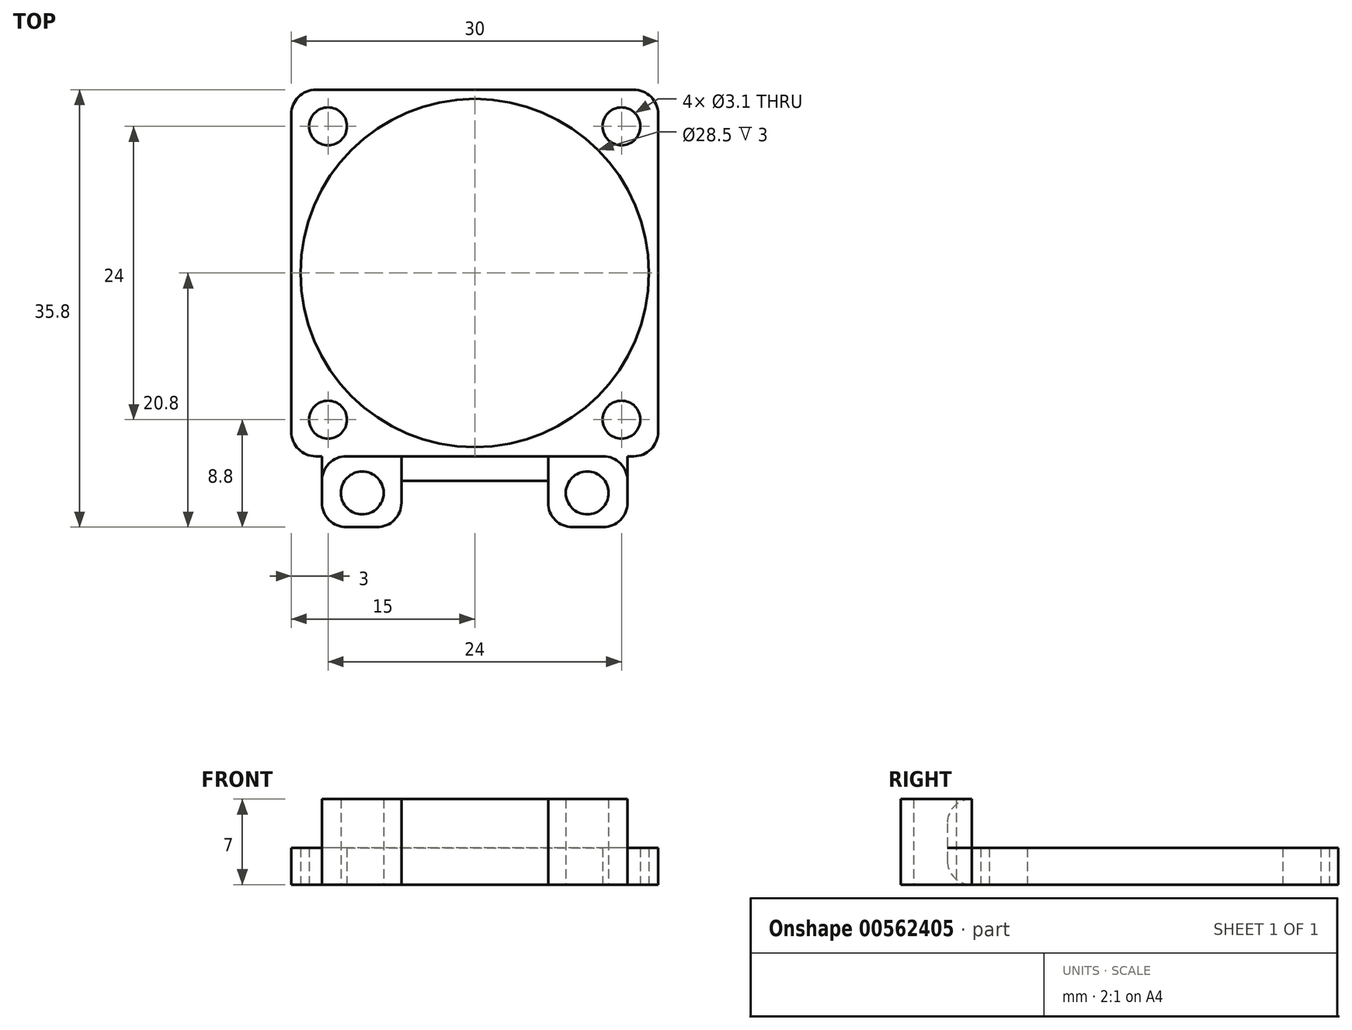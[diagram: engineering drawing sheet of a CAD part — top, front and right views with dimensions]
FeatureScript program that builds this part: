
annotation { "Feature Type Name" : "Feature", "Feature Type Description" : "" }
export const myFeature = defineFeature(function(context is Context, id is Id, definition is map)
    precondition{}
    {
        {
            var Q0;
            Q0=qCreatedBy(makeId("Top.planeOp"),FACE);
            var sketch = newSketch(context, id + "F0", { "sketchPlane" : qUnion([Q0])});
            skLineSegment(sketch, "E0.bottom", {"start": v(15, -15) * mm, "end": v(-15, -15) * mm});
            skLineSegment(sketch, "E0.top", {"start": v(15, 15) * mm, "end": v(-15, 15) * mm});
            skLineSegment(sketch, "E0.left", {"start": v(15, -15) * mm, "end": v(15, 15) * mm});
            skLineSegment(sketch, "E0.right", {"start": v(-15, -15) * mm, "end": v(-15, 15) * mm});
            skPoint(sketch, "E0.middle", {"position": v(0, 0) * mm});
            skLineSegment(sketch, "E1.bottom", {"start": v(12, -12) * mm, "end": v(-12, -12) * mm, "construction": true});
            skLineSegment(sketch, "E1.top", {"start": v(12, 12) * mm, "end": v(-12, 12) * mm, "construction": true});
            skLineSegment(sketch, "E1.left", {"start": v(12, -12) * mm, "end": v(12, 12) * mm, "construction": true});
            skLineSegment(sketch, "E1.right", {"start": v(-12, -12) * mm, "end": v(-12, 12) * mm, "construction": true});
            skCircle(sketch, "E2", {"center": v(-12, 12) * mm, "radius": 1.55 * mm});
            skCircle(sketch, "E3", {"center": v(12, 12) * mm, "radius": 1.55 * mm});
            skCircle(sketch, "E4", {"center": v(12, -12) * mm, "radius": 1.55 * mm});
            skCircle(sketch, "E5", {"center": v(-12, -12) * mm, "radius": 1.55 * mm});
            skLineSegment(sketch, "E6", {"start": v(-14.96, -20.8) * mm, "end": v(-6, -20.8) * mm, "construction": true});
            skLineSegment(sketch, "E7.bottom", {"start": v(-15, -15) * mm, "end": v(15, -15) * mm});
            skLineSegment(sketch, "E7.top", {"start": v(-6, -17) * mm, "end": v(6, -17) * mm});
            skLineSegment(sketch, "E8.bottom", {"start": v(-12.5, -15) * mm, "end": v(12.5, -15) * mm});
            skLineSegment(sketch, "E8.top", {"start": v(-12.5, -20.8) * mm, "end": v(-6, -20.8) * mm});
            skLineSegment(sketch, "E8.left", {"start": v(-12.5, -15) * mm, "end": v(-12.5, -20.8) * mm});
            skLineSegment(sketch, "E8.right", {"start": v(12.5, -15) * mm, "end": v(12.5, -20.8) * mm});
            skLineSegment(sketch, "E9.bottom", {"start": v(-6, -15) * mm, "end": v(6, -15) * mm});
            skLineSegment(sketch, "E9.left", {"start": v(-6, -15) * mm, "end": v(-6, -20.8) * mm});
            skLineSegment(sketch, "E9.right", {"start": v(6, -15) * mm, "end": v(6, -20.8) * mm});
            skPoint(sketch, "E7.right.end.orphan", {"position": v(15, -17) * mm});
            skLineSegment(sketch, "E10.trimOffspring", {"start": v(6, -20.8) * mm, "end": v(15.77, -20.8) * mm, "construction": true});
            skLineSegment(sketch, "E11.trimOffspring", {"start": v(6, -20.8) * mm, "end": v(12.5, -20.8) * mm});
            skLineSegment(sketch, "E12", {"start": v(-13.8, -18) * mm, "end": v(14.7, -18) * mm, "construction": true});
            skLineSegment(sketch, "E13", {"start": v(-9.2, -15) * mm, "end": v(-9.2, -21.94) * mm, "construction": true});
            skLineSegment(sketch, "E14", {"start": v(9.2, -15) * mm, "end": v(9.2, -21.94) * mm, "construction": true});
            skCircle(sketch, "E15", {"center": v(-9.2, -18) * mm, "radius": 1.75 * mm});
            skCircle(sketch, "E16", {"center": v(9.2, -18) * mm, "radius": 1.75 * mm});
            skCircle(sketch, "E17", {"center": v(0, 0) * mm, "radius": 14.25 * mm});
            skSolve(sketch);
        }
        {
            var Q0;
            Q0=makeQuery(id+"F0.imprint","IMPRINT",FACE,{"disambiguationData":[TD([[makeQuery(id+"F0.imprint","IMPRINT",EDGE,{"derivedFrom":sQuery(id+"F0.wireOp",EDGE,"E0.top")}),1.0]])]});
            var Q1;
            {var subQ4=sQuery(id+"F0.wireOp",EDGE,"E8.top");Q1=makeQuery(id+"F0.imprint","IMPRINT",FACE,{"disambiguationData":[TD([[makeQuery(id+"F0.imprint","IMPRINT",EDGE,{"derivedFrom":subQ4}),1.0]])]});}
            var Q2;
            {var subQ0=sQuery(id+"F0.wireOp",EDGE,"E7.top");Q2=makeQuery(id+"F0.imprint","IMPRINT",FACE,{"disambiguationData":[TD([[makeQuery(id+"F0.imprint","IMPRINT",EDGE,{"derivedFrom":subQ0}),1.0]])]});}
            var Q3;
            {var subQ5=sQuery(id+"F0.wireOp",EDGE,"E8.right");Q3=makeQuery(id+"F0.imprint","IMPRINT",FACE,{"disambiguationData":[TD([[makeQuery(id+"F0.imprint","IMPRINT",EDGE,{"derivedFrom":subQ5}),-1.0]])]});}
            extrude(context, id + "F1", {"entities" : qUnion([Q0, Q1, Q2, Q3]), "depth" : 3 * mm, "offsetDistance" : 25 * mm});
        }
        {
            var Q0;
            {var subQ0=sQuery(id+"F0.wireOp",EDGE,"E7.top");Q0=makeQuery(id+"F0.imprint","IMPRINT",FACE,{"disambiguationData":[TD([[makeQuery(id+"F0.imprint","IMPRINT",EDGE,{"derivedFrom":subQ0}),1.0]])]});}
            var Q1;
            {var subQ4=sQuery(id+"F0.wireOp",EDGE,"E8.top");Q1=makeQuery(id+"F0.imprint","IMPRINT",FACE,{"disambiguationData":[TD([[makeQuery(id+"F0.imprint","IMPRINT",EDGE,{"derivedFrom":subQ4}),1.0]])]});}
            var Q2;
            {var subQ5=sQuery(id+"F0.wireOp",EDGE,"E8.right");Q2=makeQuery(id+"F0.imprint","IMPRINT",FACE,{"disambiguationData":[TD([[makeQuery(id+"F0.imprint","IMPRINT",EDGE,{"derivedFrom":subQ5}),-1.0]])]});}
            extrude(context, id + "F2", {"entities" : qUnion([Q0, Q1, Q2]), "operationType" : NewBodyOperationType.ADD, "depth" : 7 * mm});
        }
        {
            var Q0;
            Q0=makeQuery(id+"F1.opExtrude","SWEPT_EDGE",EDGE,{"disambiguationData":[OSD([sQuery(id+"F0.wireOp",EDGE,"E0.left"),sQuery(id+"F0.wireOp",EDGE,"E7.bottom")])]});
            var Q1;
            Q1=makeQuery(id+"F1.opExtrude","SWEPT_EDGE",EDGE,{"disambiguationData":[OSD([sQuery(id+"F0.wireOp",EDGE,"E0.right"),sQuery(id+"F0.wireOp",EDGE,"E7.bottom")])]});
            var Q2;
            Q2=makeQuery(id+"F1.opExtrude","SWEPT_EDGE",EDGE,{"disambiguationData":[OSD([sQuery(id+"F0.wireOp",EDGE,"E0.top"),sQuery(id+"F0.wireOp",EDGE,"E0.right")])]});
            var Q3;
            Q3=makeQuery(id+"F1.opExtrude","SWEPT_EDGE",EDGE,{"disambiguationData":[OSD([sQuery(id+"F0.wireOp",EDGE,"E0.top"),sQuery(id+"F0.wireOp",EDGE,"E0.left")])]});
            var Q4;
            {var subQ0=sQuery(id+"F0.wireOp",EDGE,"E8.left");var subQ1=sQuery(id+"F0.wireOp",EDGE,"E8.top");Q4=makeQuery(id+"F2.boolean.opBoolean","MERGE",EDGE,{"derivedFrom":[makeQuery(id+"F1.opExtrude","SWEPT_EDGE",EDGE,{"disambiguationData":[OSD([subQ1,subQ0])]}),makeQuery(id+"F2.opExtrude","SWEPT_EDGE",EDGE,{"disambiguationData":[OSD([subQ1,subQ0])]})]});}
            var Q5;
            {var subQ0=sQuery(id+"F0.wireOp",EDGE,"E9.left");var subQ1=sQuery(id+"F0.wireOp",EDGE,"E8.top");Q5=makeQuery(id+"F2.boolean.opBoolean","MERGE",EDGE,{"derivedFrom":[makeQuery(id+"F1.opExtrude","SWEPT_EDGE",EDGE,{"disambiguationData":[OSD([subQ1,subQ0])]}),makeQuery(id+"F2.opExtrude","SWEPT_EDGE",EDGE,{"disambiguationData":[OSD([subQ1,subQ0])]})]});}
            var Q6;
            {var subQ0=sQuery(id+"F0.wireOp",EDGE,"E11.trimOffspring");var subQ1=sQuery(id+"F0.wireOp",EDGE,"E9.right");Q6=makeQuery(id+"F2.boolean.opBoolean","MERGE",EDGE,{"derivedFrom":[makeQuery(id+"F1.opExtrude","SWEPT_EDGE",EDGE,{"disambiguationData":[OSD([subQ1,subQ0])]}),makeQuery(id+"F2.opExtrude","SWEPT_EDGE",EDGE,{"disambiguationData":[OSD([subQ1,subQ0])]})]});}
            var Q7;
            {var subQ0=sQuery(id+"F0.wireOp",EDGE,"E11.trimOffspring");var subQ1=sQuery(id+"F0.wireOp",EDGE,"E8.right");Q7=makeQuery(id+"F2.boolean.opBoolean","MERGE",EDGE,{"derivedFrom":[makeQuery(id+"F1.opExtrude","SWEPT_EDGE",EDGE,{"disambiguationData":[OSD([subQ1,subQ0])]}),makeQuery(id+"F2.opExtrude","SWEPT_EDGE",EDGE,{"disambiguationData":[OSD([subQ1,subQ0])]})]});}
            var Q8;
            Q8=makeQuery(id+"F2.opExtrude","SWEPT_EDGE",EDGE,{"disambiguationData":[OSD([sQuery(id+"F0.wireOp",EDGE,"E7.bottom"),sQuery(id+"F0.wireOp",EDGE,"E8.bottom"),sQuery(id+"F0.wireOp",EDGE,"E8.right")])]});
            var Q9;
            Q9=makeQuery(id+"F2.opExtrude","SWEPT_EDGE",EDGE,{"disambiguationData":[OSD([sQuery(id+"F0.wireOp",EDGE,"E7.bottom"),sQuery(id+"F0.wireOp",EDGE,"E8.bottom"),sQuery(id+"F0.wireOp",EDGE,"E8.left")])]});
            var Q10;
            Q10=makeQuery(id+"F2.opExtrude","CAP_EDGE",EDGE,{"disambiguationData":[OSD([sQuery(id+"F0.wireOp",EDGE,"E7.top")])],"isStart":false});
            var Q11;
            Q11=makeQuery(id+"F1.opExtrude","CAP_EDGE",EDGE,{"disambiguationData":[OSD([sQuery(id+"F0.wireOp",EDGE,"E7.top")])],"isStart":true});
            fillet(context, id + "F3", {"entities" : qUnion([Q0, Q1, Q2, Q3, Q4, Q5, Q6, Q7, Q8, Q9, Q10, Q11]), "radius" : 2 * mm, "tangentPropagation" : true, "allowEdgeOverflow" : false});
        }
    });
